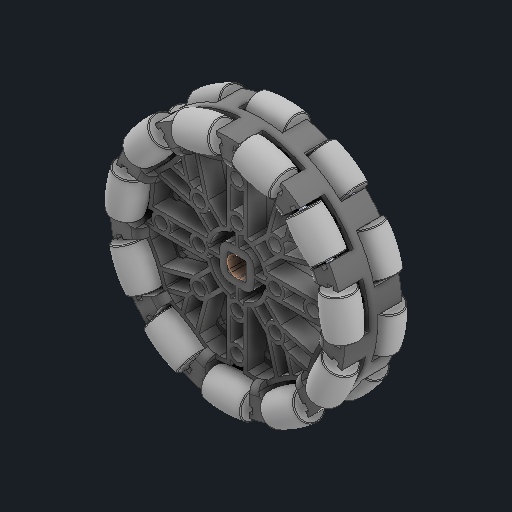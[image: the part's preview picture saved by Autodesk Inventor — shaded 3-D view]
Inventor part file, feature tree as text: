
AUTODESK INVENTOR PART (.ipt)
format: ipt  version: 2024 (Build 280153000, 153)  size: 3,336,192 bytes
history: native  units: in
note: dims shown in document units (in); Inventor stores cm internally (conversion verified against a paired STEP export)
features: other x49, sketch x1
ambient origin geometry x8: Origin, YZ Plane, XZ Plane, XY Plane, X Axis, Y Axis, Z Axis, Center Point
bodies: Solid1 (feature_tree), Solid2 (feature_tree), Solid3 (feature_tree), Solid4 (feature_tree), Solid5 (feature_tree), Solid6 (feature_tree), Solid7 (feature_tree), Solid8 (feature_tree), Solid9 (feature_tree), Solid10 (feature_tree), Solid11 (feature_tree), Solid12 (feature_tree), Solid13 (feature_tree), Solid14 (feature_tree), Solid15 (feature_tree), Solid16 (feature_tree), Solid17 (feature_tree), Solid18 (feature_tree), Solid19 (feature_tree), Solid20 (feature_tree), Solid21 (feature_tree), Solid22 (feature_tree), Solid23 (feature_tree), Solid24 (feature_tree), Solid25 (feature_tree), Solid26 (feature_tree), Solid27 (feature_tree), Solid28 (feature_tree), Solid29 (feature_tree), Solid30 (feature_tree), Solid31 (feature_tree), Solid32 (feature_tree), Solid33 (feature_tree), Solid34 (feature_tree), Solid35 (feature_tree), Solid36 (feature_tree), Solid37 (feature_tree), Solid38 (feature_tree), Solid39 (feature_tree), Solid40 (feature_tree), Solid41 (feature_tree), Solid42 (feature_tree), Solid43 (feature_tree), Solid44 (feature_tree), Solid45 (feature_tree)
feature tree (50):
  other  "3.25 Omni Antistatic.ipt"
  other  "Solid1::3.25 Omni Antistatic.ipt"
  other  "Solid2::3.25 Omni Antistatic.ipt"
  other  "Solid3::3.25 Omni Antistatic.ipt"
  other  "Solid4::3.25 Omni Antistatic.ipt"
  other  "Solid5::3.25 Omni Antistatic.ipt"
  other  "Solid6::3.25 Omni Antistatic.ipt"
  other  "Solid7::3.25 Omni Antistatic.ipt"
  other  "Solid8::3.25 Omni Antistatic.ipt"
  other  "Solid9::3.25 Omni Antistatic.ipt"
  other  "Solid10::3.25 Omni Antistatic.ipt"
  other  "Solid11::3.25 Omni Antistatic.ipt"
  other  "Solid12::3.25 Omni Antistatic.ipt"
  other  "Solid13::3.25 Omni Antistatic.ipt"
  other  "Solid14::3.25 Omni Antistatic.ipt"
  other  "Solid15::3.25 Omni Antistatic.ipt"
  other  "Solid16::3.25 Omni Antistatic.ipt"
  other  "Solid17::3.25 Omni Antistatic.ipt"
  other  "Solid18::3.25 Omni Antistatic.ipt"
  other  "Solid19::3.25 Omni Antistatic.ipt"
  other  "Solid20::3.25 Omni Antistatic.ipt"
  other  "Solid21::3.25 Omni Antistatic.ipt"
  other  "Solid22::3.25 Omni Antistatic.ipt"
  other  "Solid23::3.25 Omni Antistatic.ipt"
  other  "Solid24::3.25 Omni Antistatic.ipt"
  other  "Solid25::3.25 Omni Antistatic.ipt"
  other  "Solid26::3.25 Omni Antistatic.ipt"
  other  "Solid27::3.25 Omni Antistatic.ipt"
  other  "Solid28::3.25 Omni Antistatic.ipt"
  other  "Solid29::3.25 Omni Antistatic.ipt"
  other  "Solid30::3.25 Omni Antistatic.ipt"
  other  "Solid31::3.25 Omni Antistatic.ipt"
  other  "Solid32::3.25 Omni Antistatic.ipt"
  other  "Solid33::3.25 Omni Antistatic.ipt"
  other  "Solid34::3.25 Omni Antistatic.ipt"
  other  "Solid35::3.25 Omni Antistatic.ipt"
  other  "Solid36::3.25 Omni Antistatic.ipt"
  other  "Solid37::3.25 Omni Antistatic.ipt"
  other  "Solid38::3.25 Omni Antistatic.ipt"
  other  "Solid39::3.25 Omni Antistatic.ipt"
  other  "Solid40::3.25 Omni Antistatic.ipt"
  other  "Solid41::3.25 Omni Antistatic.ipt"
  other  "Solid42::3.25 Omni Antistatic.ipt"
  other  "Solid43::3.25 Omni Antistatic.ipt"
  other  "Solid44::3.25 Omni Antistatic.ipt"
  other  "Solid45::3.25 Omni Antistatic.ipt"
  other  "TaggingFeature1"
  sketch  "Sketch1"  dims[d0=0.3937in]
  other  "Srf1"
  other  "Srf1::Derived"
